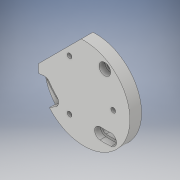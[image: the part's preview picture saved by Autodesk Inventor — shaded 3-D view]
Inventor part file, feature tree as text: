
AUTODESK INVENTOR PART (.ipt)
format: ipt  version: 2018 (Build 220112000, 112)  size: 236,544 bytes
history: native  units: in
note: dims shown in document units (in); Inventor stores cm internally (conversion verified against a paired STEP export)
features: extrude x15, sketch x9
ambient origin geometry x8: Origin, YZ Plane, XZ Plane, XY Plane, X Axis, Y Axis, Z Axis, Center Point
bodies: Solid1 (feature_tree)
feature tree (24):
  extrude  "Extrusion1"  Depth=0.2362in
  sketch  "Sketch2"  dims[d9=0.2362in d10=0.2362in]
  extrude  "Extrusion2"  Depth=0.2362in
  extrude  "Extrusion3"  Depth=0.3937in
  extrude  "Extrusion4"  Depth=0.3937in
  sketch  "Sketch3"  dims[d11=0.3937in d12=0.0in d13=0.3937in]
  extrude  "Extrusion5"  Depth=0.1969in TaperAngle=0.0deg
  extrude  "Extrusion6"  Depth=0.1575in
  extrude  "Extrusion7"  Depth=0.3937in TaperAngle=0.0deg
  sketch  "Sketch4"  dims[d14=0.3937in d15=0.3937in]
  extrude  "Extrusion8"  Depth=0.3937in TaperAngle=0.0deg
  extrude  "Extrusion9"  Depth=0.1969in
  extrude  "Extrusion10"  Depth=0.1969in
  sketch  "Sketch5"  dims[d16=0.1969in d17=0.0in d18=0.1969in d19=0.0in]
  extrude  "Extrusion11"  Depth=0.1969in TaperAngle=0.0deg
  sketch  "Sketch6"  dims[d20=0.1969in d21=0.0in d24=0.1575in]
  extrude  "Extrusion14"  Depth=0.1969in TaperAngle=0.0deg
  extrude  "Extrusion15"  Depth=0.1969in TaperAngle=0.0deg
  extrude  "Extrusion16"  Depth=0.3937in
  extrude  "Extrusion17"  Depth=0.1969in TaperAngle=0.0deg
  sketch  "Sketch1"  dims[d0=3.0906in d6=0.2362in]
  sketch  "Sketch7"  dims[d25=1.1811in d27=360.0deg d29=0.3937in d30=0.0in]
  sketch  "Sketch8"  dims[d31=0.3937in d32=0.0in d33=0.3937in d34=0.0in]
  sketch  "Sketch9"  dims[d35=0.315in d36=0.315in d37=0.315in d38=0.1969in d39=0.0in d40=0.1969in d41=0.0in d42=0.1969in d43=0.0in d57=0.3937in d62=0.1969in d63=0.0in d69=4.1732in d70=0.2362in d71=0.2362in d74=0.1969in d75=0.0in d77=135.0deg d78=0.3937in d79=0.0in d84=0.3937in d87=0.3937in d88=0.1969in d89=0.0in d90=0.2362in d92=0.2362in d93=0.1969in d94=0.0in]
